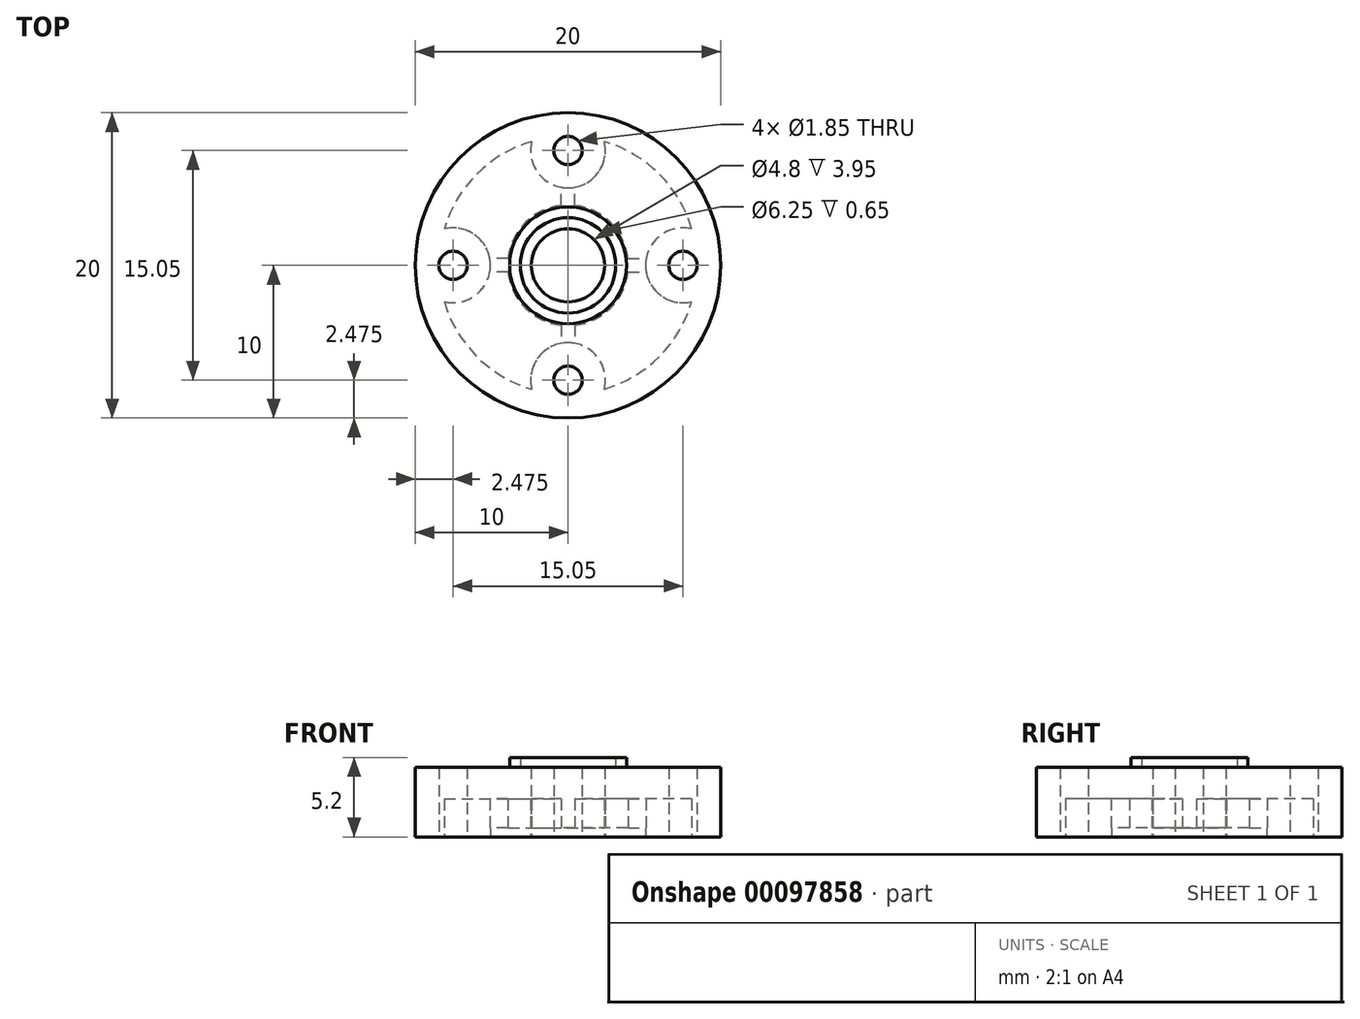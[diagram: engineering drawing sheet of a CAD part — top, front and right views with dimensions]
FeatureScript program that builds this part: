
annotation { "Feature Type Name" : "Feature", "Feature Type Description" : "" }
export const myFeature = defineFeature(function(context is Context, id is Id, definition is map)
    precondition{}
    {
        {
            var Q0;
            Q0=qCreatedBy(makeId("Top.planeOp"),FACE);
            var sketch = newSketch(context, id + "F0", { "sketchPlane" : qUnion([Q0])});
            skCircle(sketch, "E0", {"center": v(0, 0) * mm, "radius": 10 * mm});
            skSolve(sketch);
        }
        {
            var Q0;
            Q0 = qSketchRegion(id + "F0", true);
            extrude(context, id + "F1", {"entities" : qUnion([Q0]), "depth" : 4.55 * mm});
        }
        {
            var Q0;
            Q0=makeQuery(id+"F1.opExtrude","CAP_FACE",FACE,{"disambiguationData":[OSD([sQuery(id+"F0.wireOp",EDGE,"E0")])],"isStart":true});
            var sketch = newSketch(context, id + "F2", { "sketchPlane" : qUnion([Q0])});
            skCircle(sketch, "E1", {"center": v(0, 0) * mm, "radius": 8.45 * mm});
            skCircle(sketch, "E2", {"center": v(0, 0) * mm, "radius": 3.95 * mm});
            skCircle(sketch, "E3", {"center": v(0, 0) * mm, "radius": 2.4 * mm});
            skLineSegment(sketch, "E4", {"start": v(0, 8.45) * mm, "end": v(0, -8.45) * mm, "construction": true});
            skLineSegment(sketch, "E5", {"start": v(8.45, 0) * mm, "end": v(-8.45, 0) * mm, "construction": true});
            skLineSegment(sketch, "E6", {"start": v(0.45, 3.92) * mm, "end": v(0.45, 5.12) * mm});
            skLineSegment(sketch, "E7", {"start": v(-0.45, 3.92) * mm, "end": v(-0.45, 5.12) * mm});
            skLineSegment(sketch, "E8", {"start": v(3.92, 0.45) * mm, "end": v(5.12, 0.45) * mm});
            skLineSegment(sketch, "E9", {"start": v(3.92, -0.45) * mm, "end": v(5.12, -0.45) * mm});
            skLineSegment(sketch, "E10", {"start": v(0.45, -3.92) * mm, "end": v(0.45, -5.12) * mm});
            skLineSegment(sketch, "E11", {"start": v(-0.45, -3.92) * mm, "end": v(-0.45, -5.12) * mm});
            skLineSegment(sketch, "E12", {"start": v(-3.92, -0.45) * mm, "end": v(-5.12, -0.45) * mm});
            skLineSegment(sketch, "E13", {"start": v(-3.92, 0.45) * mm, "end": v(-5.12, 0.45) * mm});
            skCircle(sketch, "E14", {"center": v(7.52, 0) * mm, "radius": 0.93 * mm});
            skCircle(sketch, "E15", {"center": v(7.52, 0) * mm, "radius": 2.45 * mm});
            skCircle(sketch, "E16.1.0", {"center": v(0, 7.52) * mm, "radius": 0.93 * mm});
            skCircle(sketch, "E16.1.1", {"center": v(0, 7.52) * mm, "radius": 2.45 * mm});
            skCircle(sketch, "E16.2.0", {"center": v(-7.52, 0) * mm, "radius": 0.93 * mm});
            skCircle(sketch, "E16.2.1", {"center": v(-7.52, 0) * mm, "radius": 2.45 * mm});
            skCircle(sketch, "E16.3.0", {"center": v(0, -7.52) * mm, "radius": 0.93 * mm});
            skCircle(sketch, "E16.3.1", {"center": v(0, -7.52) * mm, "radius": 2.45 * mm});
            skLineSegment(sketch, "E17.trimOffspring", {"start": v(8.33, -0.45) * mm, "end": v(8.44, -0.45) * mm});
            skLineSegment(sketch, "E18.trimOffspring", {"start": v(8.33, 0.45) * mm, "end": v(8.44, 0.45) * mm});
            skLineSegment(sketch, "E19.trimOffspring", {"start": v(-0.45, -8.33) * mm, "end": v(-0.45, -8.44) * mm});
            skLineSegment(sketch, "E20.trimOffspring", {"start": v(0.45, -8.33) * mm, "end": v(0.45, -8.44) * mm});
            skLineSegment(sketch, "E21.trimOffspring", {"start": v(-8.33, -0.45) * mm, "end": v(-8.44, -0.45) * mm});
            skLineSegment(sketch, "E22.trimOffspring", {"start": v(-8.33, 0.45) * mm, "end": v(-8.44, 0.45) * mm});
            skLineSegment(sketch, "E23.trimOffspring", {"start": v(-0.45, 8.33) * mm, "end": v(-0.45, 8.44) * mm});
            skLineSegment(sketch, "E24.trimOffspring", {"start": v(0.45, 8.33) * mm, "end": v(0.45, 8.44) * mm});
            skSolve(sketch);
        }
        {
            var Q0;
            {var subQ6=sQuery(id+"F2.wireOp",EDGE,"E6");Q0=makeQuery(id+"F2.imprint","IMPRINT",FACE,{"disambiguationData":[TD([[makeQuery(id+"F2.imprint","IMPRINT",EDGE,{"derivedFrom":subQ6}),-1.0]])]});}
            var Q1;
            {var subQ6=sQuery(id+"F2.wireOp",EDGE,"E7");Q1=makeQuery(id+"F2.imprint","IMPRINT",FACE,{"disambiguationData":[TD([[makeQuery(id+"F2.imprint","IMPRINT",EDGE,{"derivedFrom":subQ6}),1.0]])]});}
            var Q2;
            {var subQ0=sQuery(id+"F2.wireOp",EDGE,"E11");Q2=makeQuery(id+"F2.imprint","IMPRINT",FACE,{"disambiguationData":[TD([[makeQuery(id+"F2.imprint","IMPRINT",EDGE,{"derivedFrom":subQ0}),-1.0]])]});}
            var Q3;
            {var subQ1=sQuery(id+"F2.wireOp",EDGE,"E9");Q3=makeQuery(id+"F2.imprint","IMPRINT",FACE,{"disambiguationData":[TD([[makeQuery(id+"F2.imprint","IMPRINT",EDGE,{"derivedFrom":subQ1}),-1.0]])]});}
            var Q4;
            {var subQ0=sQuery(id+"F2.wireOp",EDGE,"E14");var subQ1=makeQuery(id+"F2.imprint","INTERSECT",VERTEX,{"derivedFrom":[subQ0,sQuery(id+"F2.wireOp",EDGE,"E18.trimOffspring")]});Q4=makeQuery(id+"F2.imprint","IMPRINT",FACE,{"disambiguationData":[TD([[makeQuery(id+"F2.imprint","IMPRINT",EDGE,{"disambiguationData":[TD([[subQ1,1.0]])],"derivedFrom":subQ0}),1.0]])]});}
            var Q5;
            {var subQ0=sQuery(id+"F2.wireOp",EDGE,"E16.2.0");var subQ1=makeQuery(id+"F2.imprint","INTERSECT",VERTEX,{"derivedFrom":[subQ0,sQuery(id+"F2.wireOp",EDGE,"E21.trimOffspring")]});Q5=makeQuery(id+"F2.imprint","IMPRINT",FACE,{"disambiguationData":[TD([[makeQuery(id+"F2.imprint","IMPRINT",EDGE,{"disambiguationData":[TD([[subQ1,1.0]])],"derivedFrom":subQ0}),1.0]])]});}
            var Q6;
            {var subQ0=sQuery(id+"F2.wireOp",EDGE,"E16.1.0");var subQ1=makeQuery(id+"F2.imprint","INTERSECT",VERTEX,{"derivedFrom":[subQ0,sQuery(id+"F2.wireOp",EDGE,"E23.trimOffspring")]});Q6=makeQuery(id+"F2.imprint","IMPRINT",FACE,{"disambiguationData":[TD([[makeQuery(id+"F2.imprint","IMPRINT",EDGE,{"disambiguationData":[TD([[subQ1,1.0]])],"derivedFrom":subQ0}),1.0]])]});}
            var Q7;
            {var subQ0=sQuery(id+"F2.wireOp",EDGE,"E16.3.0");var subQ1=makeQuery(id+"F2.imprint","INTERSECT",VERTEX,{"derivedFrom":[subQ0,sQuery(id+"F2.wireOp",EDGE,"E20.trimOffspring")]});Q7=makeQuery(id+"F2.imprint","IMPRINT",FACE,{"disambiguationData":[TD([[makeQuery(id+"F2.imprint","IMPRINT",EDGE,{"disambiguationData":[TD([[subQ1,1.0]])],"derivedFrom":subQ0}),1.0]])]});}
            var Q8;
            Q8=makeQuery(id+"F2.imprint","IMPRINT",FACE,{"disambiguationData":[TD([[makeQuery(id+"F2.imprint","IMPRINT",EDGE,{"derivedFrom":sQuery(id+"F2.wireOp",EDGE,"E3")}),1.0]])]});
            extrude(context, id + "F3", {"entities" : qUnion([Q0, Q1, Q2, Q3, Q4, Q5, Q6, Q7, Q8]), "operationType" : NewBodyOperationType.REMOVE, "oppositeDirection" : true, "depth" : 2.5 * mm});
        }
        {
            var Q0;
            Q0=makeQuery(id+"F3.boolean.opBoolean","COPY",FACE,{"derivedFrom":makeQuery(id+"F3.opExtrude","CAP_FACE",FACE,{"disambiguationData":[OSD([sQuery(id+"F2.wireOp",EDGE,"E14")])],"isStart":false})});
            var Q1;
            Q1=makeQuery(id+"F3.boolean.opBoolean","COPY",FACE,{"derivedFrom":makeQuery(id+"F3.opExtrude","CAP_FACE",FACE,{"disambiguationData":[OSD([sQuery(id+"F2.wireOp",EDGE,"E16.2.0")])],"isStart":false})});
            var Q2;
            Q2=makeQuery(id+"F3.boolean.opBoolean","COPY",FACE,{"derivedFrom":makeQuery(id+"F3.opExtrude","CAP_FACE",FACE,{"disambiguationData":[OSD([sQuery(id+"F2.wireOp",EDGE,"E16.1.0")])],"isStart":false})});
            var Q3;
            Q3=makeQuery(id+"F3.boolean.opBoolean","COPY",FACE,{"derivedFrom":makeQuery(id+"F3.opExtrude","CAP_FACE",FACE,{"disambiguationData":[OSD([sQuery(id+"F2.wireOp",EDGE,"E3")])],"isStart":false})});
            var Q4;
            Q4=makeQuery(id+"F3.boolean.opBoolean","COPY",FACE,{"derivedFrom":makeQuery(id+"F3.opExtrude","CAP_FACE",FACE,{"disambiguationData":[OSD([sQuery(id+"F2.wireOp",EDGE,"E16.3.0")])],"isStart":false})});
            extrude(context, id + "F4", {"entities" : qUnion([Q0, Q1, Q2, Q3, Q4]), "operationType" : NewBodyOperationType.REMOVE, "oppositeDirection" : true, "depth" : 25 * mm});
        }
        {
            var Q0;
            Q0=makeQuery(id+"F2.imprint","IMPRINT",FACE,{"disambiguationData":[TD([[makeQuery(id+"F2.imprint","IMPRINT",EDGE,{"derivedFrom":sQuery(id+"F2.wireOp",EDGE,"E3")}),-1.0]])]});
            var Q1;
            {var subQ0=sQuery(id+"F2.wireOp",EDGE,"E6");Q1=makeQuery(id+"F2.imprint","IMPRINT",FACE,{"disambiguationData":[TD([[makeQuery(id+"F2.imprint","IMPRINT",EDGE,{"derivedFrom":subQ0}),1.0]])]});}
            var Q2;
            {var subQ0=sQuery(id+"F2.wireOp",EDGE,"E8");Q2=makeQuery(id+"F2.imprint","IMPRINT",FACE,{"disambiguationData":[TD([[makeQuery(id+"F2.imprint","IMPRINT",EDGE,{"derivedFrom":subQ0}),-1.0]])]});}
            var Q3;
            {var subQ0=sQuery(id+"F2.wireOp",EDGE,"E10");Q3=makeQuery(id+"F2.imprint","IMPRINT",FACE,{"disambiguationData":[TD([[makeQuery(id+"F2.imprint","IMPRINT",EDGE,{"derivedFrom":subQ0}),-1.0]])]});}
            var Q4;
            {var subQ0=sQuery(id+"F2.wireOp",EDGE,"E12");Q4=makeQuery(id+"F2.imprint","IMPRINT",FACE,{"disambiguationData":[TD([[makeQuery(id+"F2.imprint","IMPRINT",EDGE,{"derivedFrom":subQ0}),-1.0]])]});}
            extrude(context, id + "F5", {"entities" : qUnion([Q0, Q1, Q2, Q3, Q4]), "operationType" : NewBodyOperationType.REMOVE, "oppositeDirection" : true, "depth" : .6 * mm});
        }
        {
            var Q0;
            Q0=makeQuery(id+"F1.opExtrude","CAP_FACE",FACE,{"disambiguationData":[OSD([sQuery(id+"F0.wireOp",EDGE,"E0")])],"isStart":false});
            var sketch = newSketch(context, id + "F6", { "sketchPlane" : qUnion([Q0])});
            skCircle(sketch, "E25", {"center": v(0, 0) * mm, "radius": 3.83 * mm});
            skCircle(sketch, "E26", {"center": v(0, 0) * mm, "radius": 3.12 * mm});
            skSolve(sketch);
        }
        {
            var Q0;
            Q0 = qSketchRegion(id + "F6", true);
            extrude(context, id + "F7", {"entities" : qUnion([Q0]), "operationType" : NewBodyOperationType.ADD, "depth" : .65 * mm});
        }
    });
